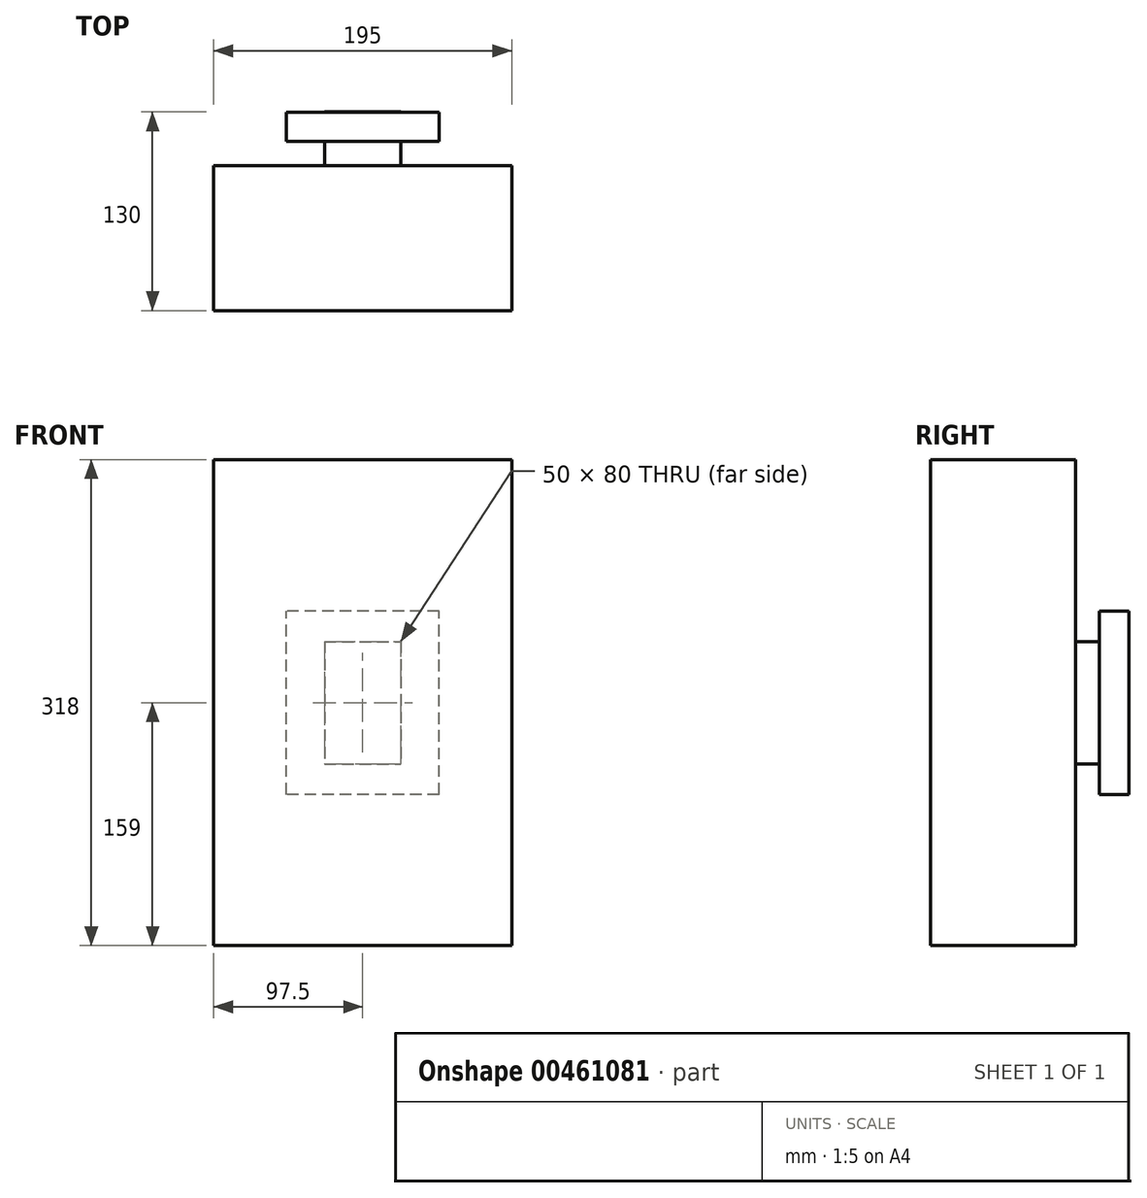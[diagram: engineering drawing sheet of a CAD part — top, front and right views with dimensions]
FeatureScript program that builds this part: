
annotation { "Feature Type Name" : "Feature", "Feature Type Description" : "" }
export const myFeature = defineFeature(function(context is Context, id is Id, definition is map)
    precondition{}
    {
        {
            var Q0;
            Q0=qCreatedBy(makeId("Front.planeOp"),FACE);
            var sketch = newSketch(context, id + "F0", { "sketchPlane" : qUnion([Q0])});
            skLineSegment(sketch, "E0.bottom", {"start": v(-97.5, 159) * mm, "end": v(97.5, 159) * mm});
            skLineSegment(sketch, "E0.top", {"start": v(-97.5, -159) * mm, "end": v(97.5, -159) * mm});
            skLineSegment(sketch, "E0.left", {"start": v(-97.5, 159) * mm, "end": v(-97.5, -159) * mm});
            skLineSegment(sketch, "E0.right", {"start": v(97.5, 159) * mm, "end": v(97.5, -159) * mm});
            skLineSegment(sketch, "E1", {"start": v(-73.04, 0) * mm, "end": v(84.3, 0) * mm, "construction": true});
            skLineSegment(sketch, "E2", {"start": v(0, 74.92) * mm, "end": v(0, -62.59) * mm, "construction": true});
            skSolve(sketch);
        }
        {
            var Q0;
            Q0=makeQuery(id+"F0.imprint","IMPRINT",FACE,{"disambiguationData":[TD([[makeQuery(id+"F0.imprint","IMPRINT",EDGE,{"derivedFrom":sQuery(id+"F0.wireOp",EDGE,"E0.bottom")}),-1.0]])]});
            extrude(context, id + "F1", {"entities" : qUnion([Q0]), "depth" : 95 * mm});
        }
        {
            var Q0;
            Q0=makeQuery(id+"F1.opExtrude","CAP_FACE",FACE,{"disambiguationData":[OSD([sQuery(id+"F0.wireOp",EDGE,"E0.bottom"),sQuery(id+"F0.wireOp",EDGE,"E0.top"),sQuery(id+"F0.wireOp",EDGE,"E0.left"),sQuery(id+"F0.wireOp",EDGE,"E0.right")])],"isStart":true});
            var sketch = newSketch(context, id + "F2", { "sketchPlane" : qUnion([Q0])});
            skLineSegment(sketch, "E3", {"start": v(-70.04, 0) * mm, "end": v(120.54, 0) * mm, "construction": true});
            skLineSegment(sketch, "E4", {"start": v(0, 90.51) * mm, "end": v(0, -100.96) * mm, "construction": true});
            skLineSegment(sketch, "E5.bottom", {"start": v(25, 40) * mm, "end": v(-25, 40) * mm});
            skLineSegment(sketch, "E5.top", {"start": v(25, -40) * mm, "end": v(-25, -40) * mm});
            skLineSegment(sketch, "E5.left", {"start": v(25, 40) * mm, "end": v(25, -40) * mm});
            skLineSegment(sketch, "E5.right", {"start": v(-25, 40) * mm, "end": v(-25, -40) * mm});
            skPoint(sketch, "E5.middle", {"position": v(0, 0) * mm});
            skLineSegment(sketch, "E6.bottom", {"start": v(-50, -60) * mm, "end": v(50, -60) * mm});
            skLineSegment(sketch, "E6.top", {"start": v(-50, 60) * mm, "end": v(50, 60) * mm});
            skLineSegment(sketch, "E6.left", {"start": v(-50, -60) * mm, "end": v(-50, 60) * mm});
            skLineSegment(sketch, "E6.right", {"start": v(50, -60) * mm, "end": v(50, 60) * mm});
            skSolve(sketch);
        }
        {
            var Q0;
            Q0=makeQuery(id+"F2.imprint","IMPRINT",FACE,{"disambiguationData":[TD([[makeQuery(id+"F2.imprint","IMPRINT",EDGE,{"derivedFrom":sQuery(id+"F2.wireOp",EDGE,"E5.bottom")}),1.0]])]});
            extrude(context, id + "F3", {"entities" : qUnion([Q0]), "operationType" : NewBodyOperationType.ADD, "depth" : 35 * mm});
        }
        {
            var Q0;
            Q0=makeQuery(id+"F2.imprint","IMPRINT",FACE,{"disambiguationData":[TD([[makeQuery(id+"F2.imprint","IMPRINT",EDGE,{"derivedFrom":sQuery(id+"F2.wireOp",EDGE,"E5.bottom")}),-1.0]])]});
            var Q1;
            Q1=makeQuery(id+"F3.opExtrude","CAP_FACE",FACE,{"disambiguationData":[OSD([sQuery(id+"F2.wireOp",EDGE,"E5.bottom"),sQuery(id+"F2.wireOp",EDGE,"E5.top"),sQuery(id+"F2.wireOp",EDGE,"E5.left"),sQuery(id+"F2.wireOp",EDGE,"E5.right")])],"isStart":false});
            var Q2;
            Q2=makeQuery(id+"F3.opExtrude","CAP_VERTEX",VERTEX,{"disambiguationData":[OSD([sQuery(id+"F2.wireOp",EDGE,"E5.top"),sQuery(id+"F2.wireOp",EDGE,"E5.right")])],"isStart":false});
            var Q3;
            Q3=makeQuery(id+"F3.opExtrude","CAP_FACE",FACE,{"disambiguationData":[OSD([sQuery(id+"F2.wireOp",EDGE,"E5.bottom"),sQuery(id+"F2.wireOp",EDGE,"E5.top"),sQuery(id+"F2.wireOp",EDGE,"E5.left"),sQuery(id+"F2.wireOp",EDGE,"E5.right")])],"isStart":false});
            extrude(context, id + "F4", {"entities" : qUnion([Q0]), "operationType" : NewBodyOperationType.ADD, "endBoundEntityFace" : qUnion([Q1]), "endBoundEntityVertex" : qUnion([Q2]), "depth" : 34.9 * mm, "hasSecondDirection" : true, "secondDirectionOppositeDirection" : false, "secondDirectionBoundEntityFace" : qUnion([Q3]), "secondDirectionDepth" : 15.7 * mm});
        }
    });
